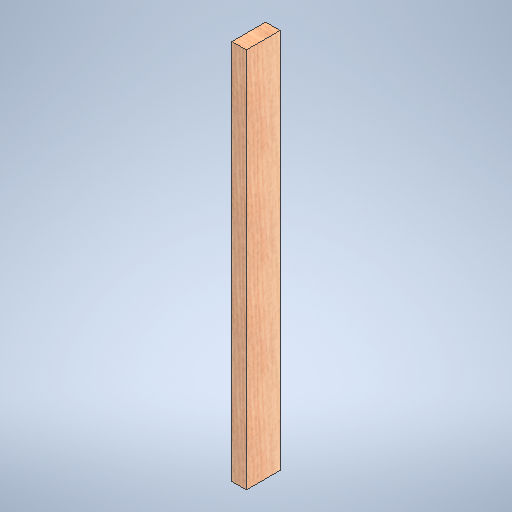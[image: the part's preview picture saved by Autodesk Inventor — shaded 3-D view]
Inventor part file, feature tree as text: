
AUTODESK INVENTOR PART (.ipt)
format: ipt  version: 2025.1 (Build 291241020, 241B)  size: 313,344 bytes
history: native  units: in
note: dims shown in document units (in); Inventor stores cm internally (conversion verified against a paired STEP export)
features: extrude x1, sketch x1
ambient origin geometry x8: Origin, YZ Plane, XZ Plane, XY Plane, X Axis, Y Axis, Z Axis, Center Point
bodies: Solid1 (feature_tree)
feature tree (2):
  extrude  "Extrusion1"  Depth=1.5in
  sketch  "Sketch1"  dims[d0=3.5in d1=1.5in d2=39.5in d3=0.0in]
